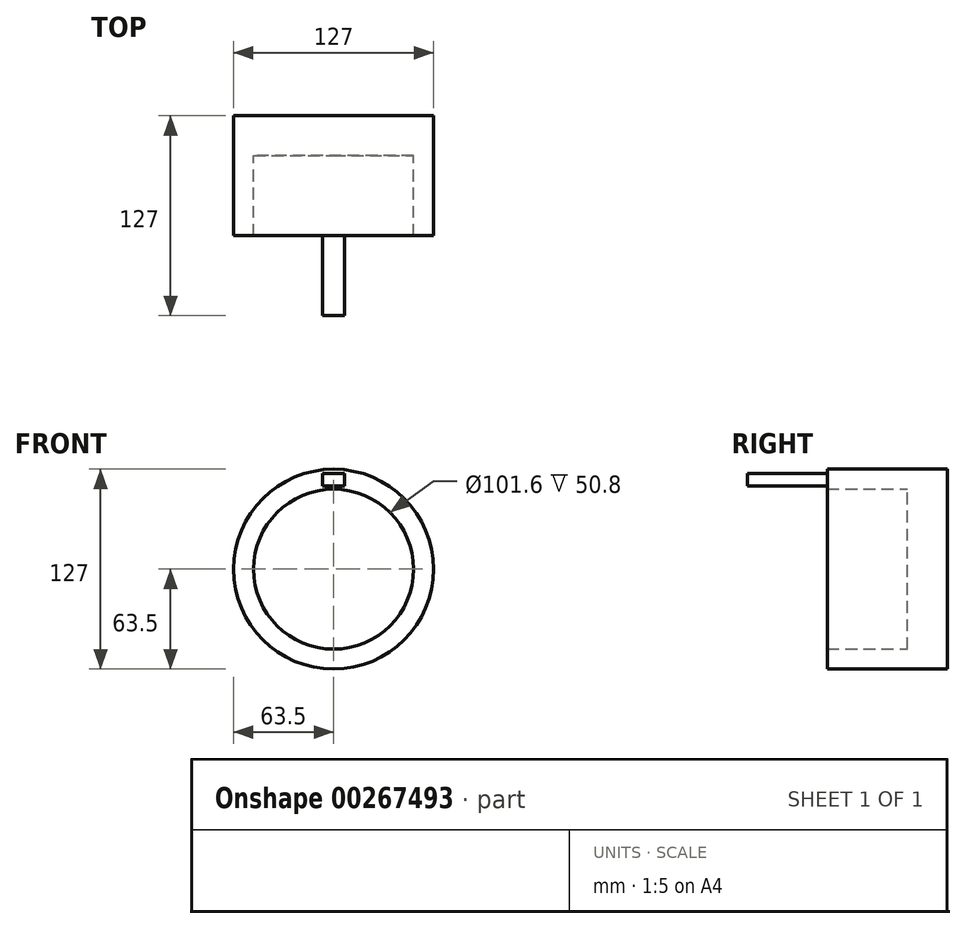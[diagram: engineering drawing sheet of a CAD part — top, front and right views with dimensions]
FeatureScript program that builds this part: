
annotation { "Feature Type Name" : "Feature", "Feature Type Description" : "" }
export const myFeature = defineFeature(function(context is Context, id is Id, definition is map)
    precondition{}
    {
        {
            var Q0;
            Q0=qCreatedBy(makeId("Front.planeOp"),FACE);
            var sketch = newSketch(context, id + "F0", { "sketchPlane" : qUnion([Q0])});
            skCircle(sketch, "E0", {"center": v(0, 0) * mm, "radius": 63.5 * mm});
            skCircle(sketch, "E1", {"center": v(0, 0) * mm, "radius": 50.8 * mm});
            skLineSegment(sketch, "E2.bottom", {"start": v(-6.86, 60.8) * mm, "end": v(6.86, 60.8) * mm});
            skLineSegment(sketch, "E2.top", {"start": v(-6.86, 52.99) * mm, "end": v(6.86, 52.99) * mm});
            skLineSegment(sketch, "E2.left", {"start": v(-6.86, 60.8) * mm, "end": v(-6.86, 52.99) * mm});
            skLineSegment(sketch, "E2.right", {"start": v(6.86, 60.8) * mm, "end": v(6.86, 52.99) * mm});
            skPoint(sketch, "E2.middle", {"position": v(0, 56.9) * mm});
            skSolve(sketch);
        }
        {
            var Q0;
            Q0=makeQuery(id+"F0.imprint","IMPRINT",FACE,{"disambiguationData":[TD([[makeQuery(id+"F0.imprint","IMPRINT",EDGE,{"derivedFrom":sQuery(id+"F0.wireOp",EDGE,"E0")}),1.0]])]});
            extrude(context, id + "F1", {"entities" : qUnion([Q0]), "depth" : 76.2 * mm});
        }
        {
            var Q0;
            Q0=makeQuery(id+"F0.imprint","IMPRINT",FACE,{"disambiguationData":[TD([[makeQuery(id+"F0.imprint","IMPRINT",EDGE,{"derivedFrom":sQuery(id+"F0.wireOp",EDGE,"E1")}),1.0]])]});
            extrude(context, id + "F2", {"entities" : qUnion([Q0]), "operationType" : NewBodyOperationType.ADD, "depth" : 25.4 * mm});
        }
        {
            var Q0;
            Q0=makeQuery(id+"F0.imprint","IMPRINT",FACE,{"disambiguationData":[TD([[makeQuery(id+"F0.imprint","IMPRINT",EDGE,{"derivedFrom":sQuery(id+"F0.wireOp",EDGE,"E2.bottom")}),-1.0]])]});
            extrude(context, id + "F3", {"entities" : qUnion([Q0]), "operationType" : NewBodyOperationType.ADD, "depth" : 127 * mm});
        }
    });
